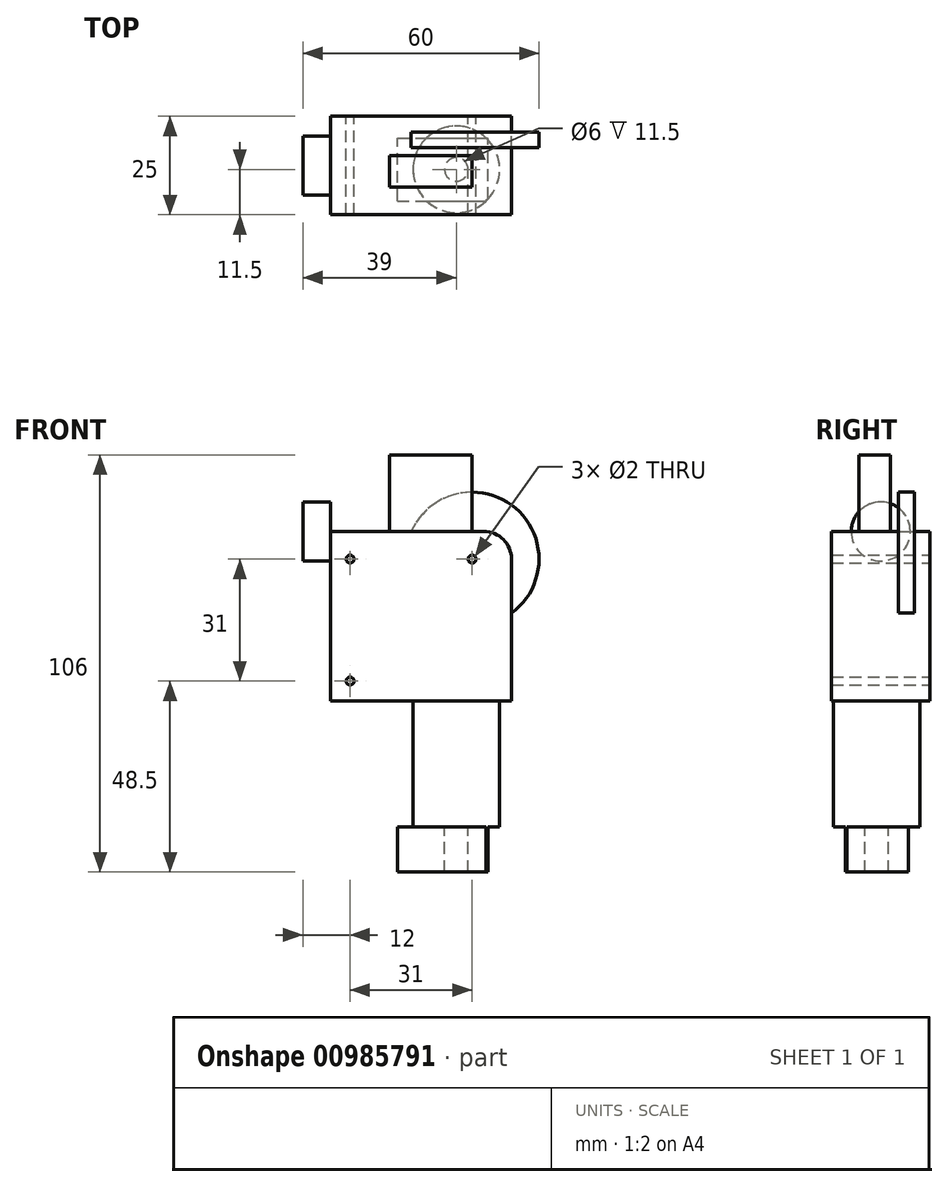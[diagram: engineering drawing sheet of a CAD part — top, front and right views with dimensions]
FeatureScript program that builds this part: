
annotation { "Feature Type Name" : "Feature", "Feature Type Description" : "" }
export const myFeature = defineFeature(function(context is Context, id is Id, definition is map)
    precondition{}
    {
        {
            var Q0;
            Q0=qCreatedBy(makeId("Front.planeOp"),FACE);
            var sketch = newSketch(context, id + "F0", { "sketchPlane" : qUnion([Q0])});
            skLineSegment(sketch, "E0.bottom", {"start": v(0, 0) * mm, "end": v(-46, 0) * mm});
            skLineSegment(sketch, "E0.top", {"start": v(0, 43) * mm, "end": v(-46, 43) * mm});
            skLineSegment(sketch, "E0.left", {"start": v(0, 0) * mm, "end": v(0, 43) * mm});
            skLineSegment(sketch, "E0.right", {"start": v(-46, 0) * mm, "end": v(-46, 43) * mm});
            skCircle(sketch, "E1", {"center": v(-41, 36) * mm, "radius": 1 * mm});
            skCircle(sketch, "E2", {"center": v(-41, 5) * mm, "radius": 1 * mm});
            skCircle(sketch, "E3", {"center": v(-10, 36) * mm, "radius": 1 * mm});
            skSolve(sketch);
        }
        {
            var Q0;
            Q0=makeQuery(id+"F0.imprint","IMPRINT",FACE,{"disambiguationData":[TD([[makeQuery(id+"F0.imprint","IMPRINT",EDGE,{"derivedFrom":sQuery(id+"F0.wireOp",EDGE,"E0.bottom")}),-1.0]])]});
            extrude(context, id + "F1", {"entities" : qUnion([Q0]), "depth" : 25 * mm, "offsetDistance" : 25 * mm});
        }
        {
            var Q0;
            Q0=makeQuery(id+"F1.opExtrude","CAP_FACE",FACE,{"disambiguationData":[OSD([sQuery(id+"F0.wireOp",EDGE,"E0.bottom"),sQuery(id+"F0.wireOp",EDGE,"E0.top"),sQuery(id+"F0.wireOp",EDGE,"E0.left"),sQuery(id+"F0.wireOp",EDGE,"E0.right"),sQuery(id+"F0.wireOp",EDGE,"E1"),sQuery(id+"F0.wireOp",EDGE,"E2"),sQuery(id+"F0.wireOp",EDGE,"E3")])],"isStart":true});
            cPlane(context, id + "F2", {"entities" : qUnion([Q0]), "cplaneType" : CPlaneType.OFFSET, "offset" : 4 * mm, "oppositeDirection" : true, "width" : 150 * mm, "height" : 150 * mm});
        }
        {
            var Q0;
            Q0=qCreatedBy(id+"F2.planeOp",FACE);
            var sketch = newSketch(context, id + "F3", { "sketchPlane" : qUnion([Q0])});
            skCircle(sketch, "E4.0", {"center": v(10, 36) * mm, "radius": 1 * mm});
            skCircle(sketch, "E5", {"center": v(10, 36) * mm, "radius": 17 * mm});
            skSolve(sketch);
        }
        {
            var Q0;
            Q0=makeQuery(id+"F1.opExtrude","SWEPT_EDGE",EDGE,{"disambiguationData":[OSD([sQuery(id+"F0.wireOp",EDGE,"E0.top"),sQuery(id+"F0.wireOp",EDGE,"E0.left")])]});
            fillet(context, id + "F4", {"entities" : qUnion([Q0]), "radius" : 7 * mm, "tangentPropagation" : true, "allowEdgeOverflow" : false});
        }
        {
            var Q0;
            Q0=makeQuery(id+"F3.imprint","IMPRINT",FACE,{"disambiguationData":[TD([[makeQuery(id+"F3.imprint","IMPRINT",EDGE,{"derivedFrom":sQuery(id+"F3.wireOp",EDGE,"E4.0")}),-1.0]])]});
            extrude(context, id + "F5", {"entities" : qUnion([Q0]), "operationType" : NewBodyOperationType.ADD, "oppositeDirection" : true, "depth" : 4 * mm, "offsetDistance" : 25 * mm});
        }
        {
            var Q0;
            Q0=makeQuery(id+"F1.opExtrude","CAP_FACE",FACE,{"disambiguationData":[OSD([sQuery(id+"F0.wireOp",EDGE,"E0.bottom"),sQuery(id+"F0.wireOp",EDGE,"E0.top"),sQuery(id+"F0.wireOp",EDGE,"E0.left"),sQuery(id+"F0.wireOp",EDGE,"E0.right"),sQuery(id+"F0.wireOp",EDGE,"E1"),sQuery(id+"F0.wireOp",EDGE,"E2"),sQuery(id+"F0.wireOp",EDGE,"E3")])],"isStart":true});
            cPlane(context, id + "F6", {"entities" : qUnion([Q0]), "cplaneType" : CPlaneType.OFFSET, "offset" : 10 * mm, "oppositeDirection" : true, "width" : 150 * mm, "height" : 150 * mm});
        }
        {
            var Q0;
            Q0=qCreatedBy(id+"F6.planeOp",FACE);
            var sketch = newSketch(context, id + "F7", { "sketchPlane" : qUnion([Q0])});
            skLineSegment(sketch, "E6.0.0", {"start": v(0, 0) * mm, "end": v(0, 36) * mm});
            skArc(sketch, "E6.0.1", {"start": v(0, 36) * mm, "mid": v(2.05, 40.95) * mm, "end": v(7, 43) * mm});
            skLineSegment(sketch, "E6.0.2", {"start": v(7, 43) * mm, "end": v(46, 43) * mm});
            skLineSegment(sketch, "E6.0.3", {"start": v(46, 43) * mm, "end": v(46, 0) * mm});
            skLineSegment(sketch, "E6.0.4", {"start": v(46, 0) * mm, "end": v(0, 0) * mm});
            skLineSegment(sketch, "E7.bottom", {"start": v(31, 43) * mm, "end": v(10, 43) * mm});
            skLineSegment(sketch, "E7.top", {"start": v(31, 62.5) * mm, "end": v(10, 62.5) * mm});
            skLineSegment(sketch, "E7.left", {"start": v(31, 43) * mm, "end": v(31, 62.5) * mm});
            skLineSegment(sketch, "E7.right", {"start": v(10, 43) * mm, "end": v(10, 62.5) * mm});
            skSolve(sketch);
        }
        {
            var Q0;
            Q0=makeQuery(id+"F7.imprint","IMPRINT",FACE,{"disambiguationData":[TD([[makeQuery(id+"F7.imprint","IMPRINT",EDGE,{"derivedFrom":sQuery(id+"F7.wireOp",EDGE,"E7.top")}),1.0]])]});
            extrude(context, id + "F8", {"entities" : qUnion([Q0]), "operationType" : NewBodyOperationType.ADD, "oppositeDirection" : true, "depth" : 8 * mm, "offsetDistance" : 25 * mm});
        }
        {
            var Q0;
            Q0=makeQuery(id+"F1.opExtrude","SWEPT_FACE",FACE,{"disambiguationData":[OSD([sQuery(id+"F0.wireOp",EDGE,"E0.right")])]});
            var sketch = newSketch(context, id + "F9", { "sketchPlane" : qUnion([Q0])});
            skLineSegment(sketch, "E8.0.0", {"start": v(0, 43) * mm, "end": v(0, 0) * mm});
            skLineSegment(sketch, "E8.0.1", {"start": v(0, 0) * mm, "end": v(25, 0) * mm});
            skLineSegment(sketch, "E8.0.2", {"start": v(25, 0) * mm, "end": v(25, 43) * mm});
            skLineSegment(sketch, "E8.0.3", {"start": v(25, 43) * mm, "end": v(0, 43) * mm});
            skCircle(sketch, "E9", {"center": v(12.5, 43) * mm, "radius": 7.5 * mm});
            skSolve(sketch);
        }
        {
            var Q0;
            {var subQ0=sQuery(id+"F9.wireOp",EDGE,"E9");var subQ1=sQuery(id+"F9.wireOp",EDGE,"E8.0.3");var subQ2=makeQuery(id+"F9.imprint","INTERSECT",VERTEX,{"disambiguationData":[OD(0.0)],"derivedFrom":[subQ1,subQ0]});Q0=makeQuery(id+"F9.imprint","IMPRINT",FACE,{"disambiguationData":[TD([[makeQuery(id+"F9.imprint","IMPRINT",EDGE,{"disambiguationData":[TD([[subQ2,-1.0]])],"derivedFrom":subQ1}),1.0]])]});}
            var Q1;
            {var subQ0=sQuery(id+"F9.wireOp",EDGE,"E9");var subQ1=sQuery(id+"F9.wireOp",EDGE,"E8.0.3");var subQ2=makeQuery(id+"F9.imprint","INTERSECT",VERTEX,{"disambiguationData":[OD(0.0)],"derivedFrom":[subQ1,subQ0]});Q1=makeQuery(id+"F9.imprint","IMPRINT",FACE,{"disambiguationData":[TD([[makeQuery(id+"F9.imprint","IMPRINT",EDGE,{"disambiguationData":[TD([[subQ2,-1.0]])],"derivedFrom":subQ1}),-1.0]])]});}
            extrude(context, id + "F10", {"entities" : qUnion([Q0, Q1]), "operationType" : NewBodyOperationType.ADD, "depth" : 7 * mm, "offsetDistance" : 25 * mm});
        }
        {
            var Q0;
            Q0=makeQuery(id+"F1.opExtrude","SWEPT_FACE",FACE,{"disambiguationData":[OSD([sQuery(id+"F0.wireOp",EDGE,"E0.bottom")])]});
            var sketch = newSketch(context, id + "F11", { "sketchPlane" : qUnion([Q0])});
            skLineSegment(sketch, "E10.0.0", {"start": v(-46, 0) * mm, "end": v(0, 0) * mm});
            skLineSegment(sketch, "E10.0.1", {"start": v(0, 0) * mm, "end": v(0, 25) * mm});
            skLineSegment(sketch, "E10.0.2", {"start": v(0, 25) * mm, "end": v(-46, 25) * mm});
            skLineSegment(sketch, "E10.0.3", {"start": v(-46, 25) * mm, "end": v(-46, 0) * mm});
            skCircle(sketch, "E11", {"center": v(-14, 13.5) * mm, "radius": 11 * mm});
            skSolve(sketch);
        }
        {
            var Q0;
            Q0=makeQuery(id+"F11.imprint","IMPRINT",FACE,{"disambiguationData":[TD([[makeQuery(id+"F11.imprint","IMPRINT",EDGE,{"derivedFrom":sQuery(id+"F11.wireOp",EDGE,"E11")}),1.0]])]});
            extrude(context, id + "F12", {"entities" : qUnion([Q0]), "operationType" : NewBodyOperationType.ADD, "depth" : 32 * mm, "offsetDistance" : 25 * mm});
        }
        {
            var Q0;
            Q0=makeQuery(id+"F12.opExtrude","CAP_FACE",FACE,{"disambiguationData":[OSD([sQuery(id+"F11.wireOp",EDGE,"E11")])],"isStart":false});
            var sketch = newSketch(context, id + "F13", { "sketchPlane" : qUnion([Q0])});
            skCircle(sketch, "E12.0.0", {"center": v(-14, 13.5) * mm, "radius": 11 * mm});
            skLineSegment(sketch, "E13.bottom", {"start": v(-29, 21.5) * mm, "end": v(-6, 21.5) * mm});
            skLineSegment(sketch, "E13.top", {"start": v(-29, 5.5) * mm, "end": v(-6, 5.5) * mm});
            skLineSegment(sketch, "E13.left", {"start": v(-29, 21.5) * mm, "end": v(-29, 5.5) * mm});
            skLineSegment(sketch, "E13.right", {"start": v(-6, 21.5) * mm, "end": v(-6, 5.5) * mm});
            skCircle(sketch, "E14", {"center": v(-14, 13.5) * mm, "radius": 3 * mm});
            skSolve(sketch);
        }
        {
            var Q0;
            {var subQ5=sQuery(id+"F13.wireOp",EDGE,"E13.left");Q0=makeQuery(id+"F13.imprint","IMPRINT",FACE,{"disambiguationData":[TD([[makeQuery(id+"F13.imprint","IMPRINT",EDGE,{"derivedFrom":subQ5}),1.0]])]});}
            var Q1;
            Q1=makeQuery(id+"F13.imprint","IMPRINT",FACE,{"disambiguationData":[TD([[makeQuery(id+"F13.imprint","IMPRINT",EDGE,{"derivedFrom":sQuery(id+"F13.wireOp",EDGE,"E14")}),-1.0]])]});
            var Q2;
            {var subQ0=sQuery(id+"F13.wireOp",EDGE,"E13.top");var subQ1=sQuery(id+"F13.wireOp",EDGE,"E12.0.0");var subQ2=makeQuery(id+"F13.imprint","INTERSECT",VERTEX,{"disambiguationData":[OD(1.0)],"derivedFrom":[subQ1,subQ0]});Q2=makeQuery(id+"F13.imprint","IMPRINT",FACE,{"disambiguationData":[TD([[makeQuery(id+"F13.imprint","IMPRINT",EDGE,{"disambiguationData":[TD([[subQ2,-1.0]])],"derivedFrom":subQ1}),-1.0]])]});}
            var Q3;
            {var subQ0=sQuery(id+"F13.wireOp",EDGE,"E13.bottom");var subQ1=sQuery(id+"F13.wireOp",EDGE,"E12.0.0");var subQ2=makeQuery(id+"F13.imprint","INTERSECT",VERTEX,{"disambiguationData":[OD(0.0)],"derivedFrom":[subQ1,subQ0]});Q3=makeQuery(id+"F13.imprint","IMPRINT",FACE,{"disambiguationData":[TD([[makeQuery(id+"F13.imprint","IMPRINT",EDGE,{"disambiguationData":[TD([[subQ2,1.0]])],"derivedFrom":subQ1}),-1.0]])]});}
            extrude(context, id + "F14", {"entities" : qUnion([Q0, Q1, Q2, Q3]), "operationType" : NewBodyOperationType.ADD, "depth" : 11.5 * mm, "offsetDistance" : 25 * mm});
        }
    });
